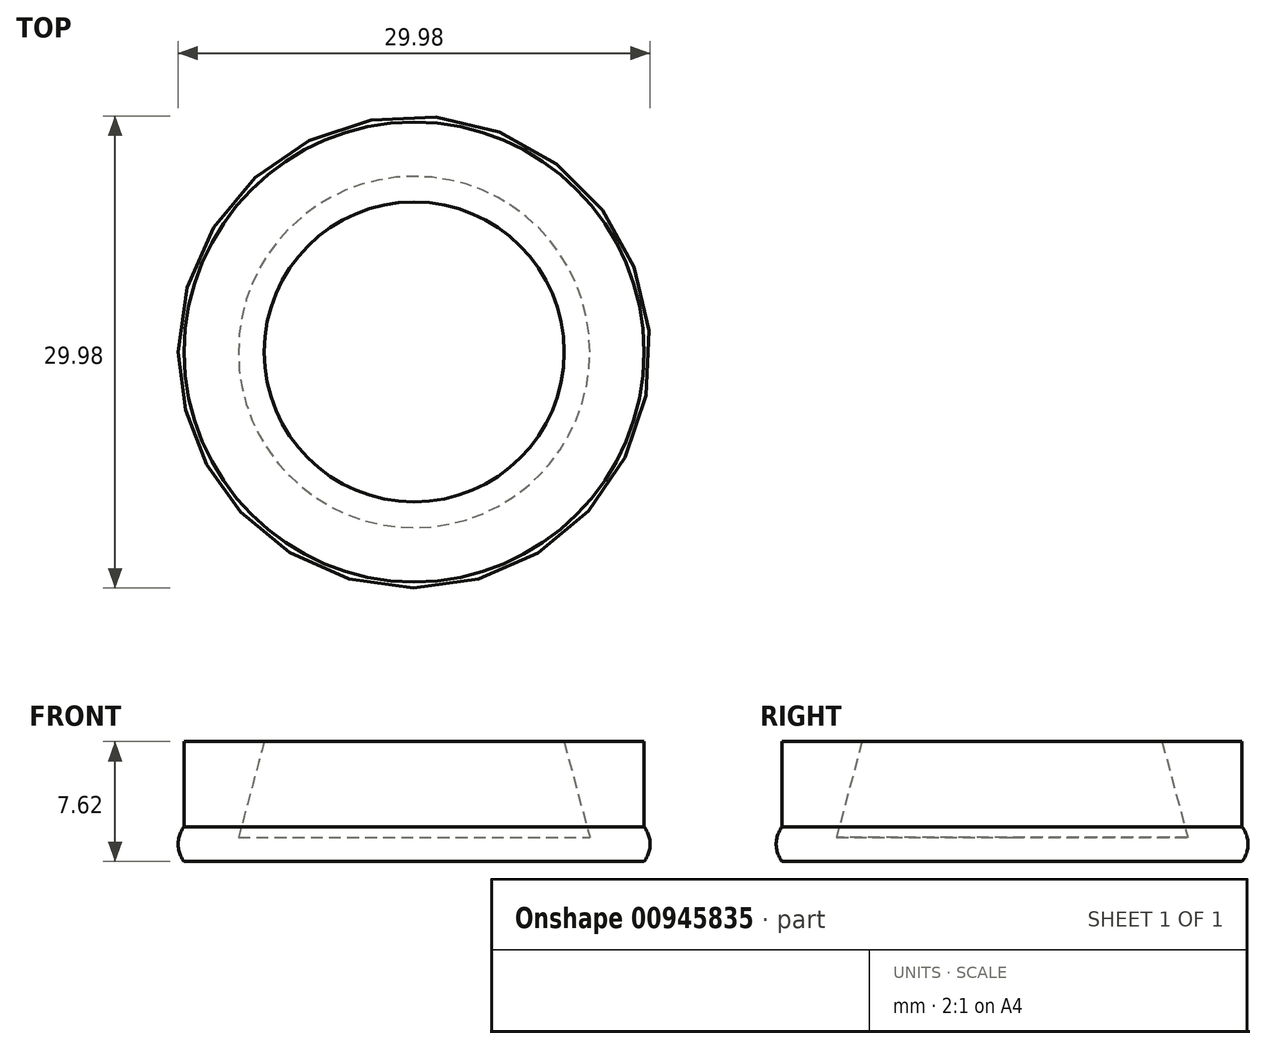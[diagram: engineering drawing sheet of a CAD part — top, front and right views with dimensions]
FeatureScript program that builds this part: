
annotation { "Feature Type Name" : "Feature", "Feature Type Description" : "" }
export const myFeature = defineFeature(function(context is Context, id is Id, definition is map)
    precondition{}
    {
        {
            var Q0;
            Q0=qCreatedBy(makeId("Front.planeOp"),FACE);
            var sketch = newSketch(context, id + "F0", { "sketchPlane" : qUnion([Q0])});
            skLineSegment(sketch, "E0", {"start": v(0, 0) * mm, "end": v(0, 1.52) * mm});
            skArc(sketch, "E1", {"start": v(-14.6, 2.2) * mm, "mid": v(-14.99, 1.1) * mm, "end": v(-14.6, 0) * mm});
            skLineSegment(sketch, "E2", {"start": v(-14.6, 0) * mm, "end": v(0, 0) * mm});
            skLineSegment(sketch, "E3", {"start": v(-14.6, 2.2) * mm, "end": v(-14.6, 7.62) * mm});
            skLineSegment(sketch, "E4", {"start": v(-14.6, 7.62) * mm, "end": v(-9.52, 7.62) * mm});
            skLineSegment(sketch, "E5", {"start": v(-9.52, 7.62) * mm, "end": v(-11.16, 1.52) * mm});
            skLineSegment(sketch, "E6", {"start": v(-11.16, 1.52) * mm, "end": v(0, 1.52) * mm});
            skLineSegment(sketch, "E7", {"start": v(-14.6, 2.2) * mm, "end": v(-14.6, 0) * mm, "construction": true});
            skSolve(sketch);
        }
        {
            var Q0;
            Q0=qCreatedBy(makeId("Front.planeOp"),FACE);
            var sketch = newSketch(context, id + "F1", { "sketchPlane" : qUnion([Q0])});
            skLineSegment(sketch, "E8", {"start": v(0, 0) * mm, "end": v(0, 5.63) * mm, "construction": true});
            skSolve(sketch);
        }
        {
            var Q0;
            Q0 = qSketchRegion(id + "F0", true);
            var Q1;
            Q1=sQuery(id+"F1.wireOp",EDGE,"E8");
            revolve(context, id + "F2", {"surfaceOperationType" : NewSurfaceOperationType.NEW, "entities" : qUnion([Q0]), "axis" : qUnion([Q1]), "revolveType" : RevolveType.FULL});
        }
    });
